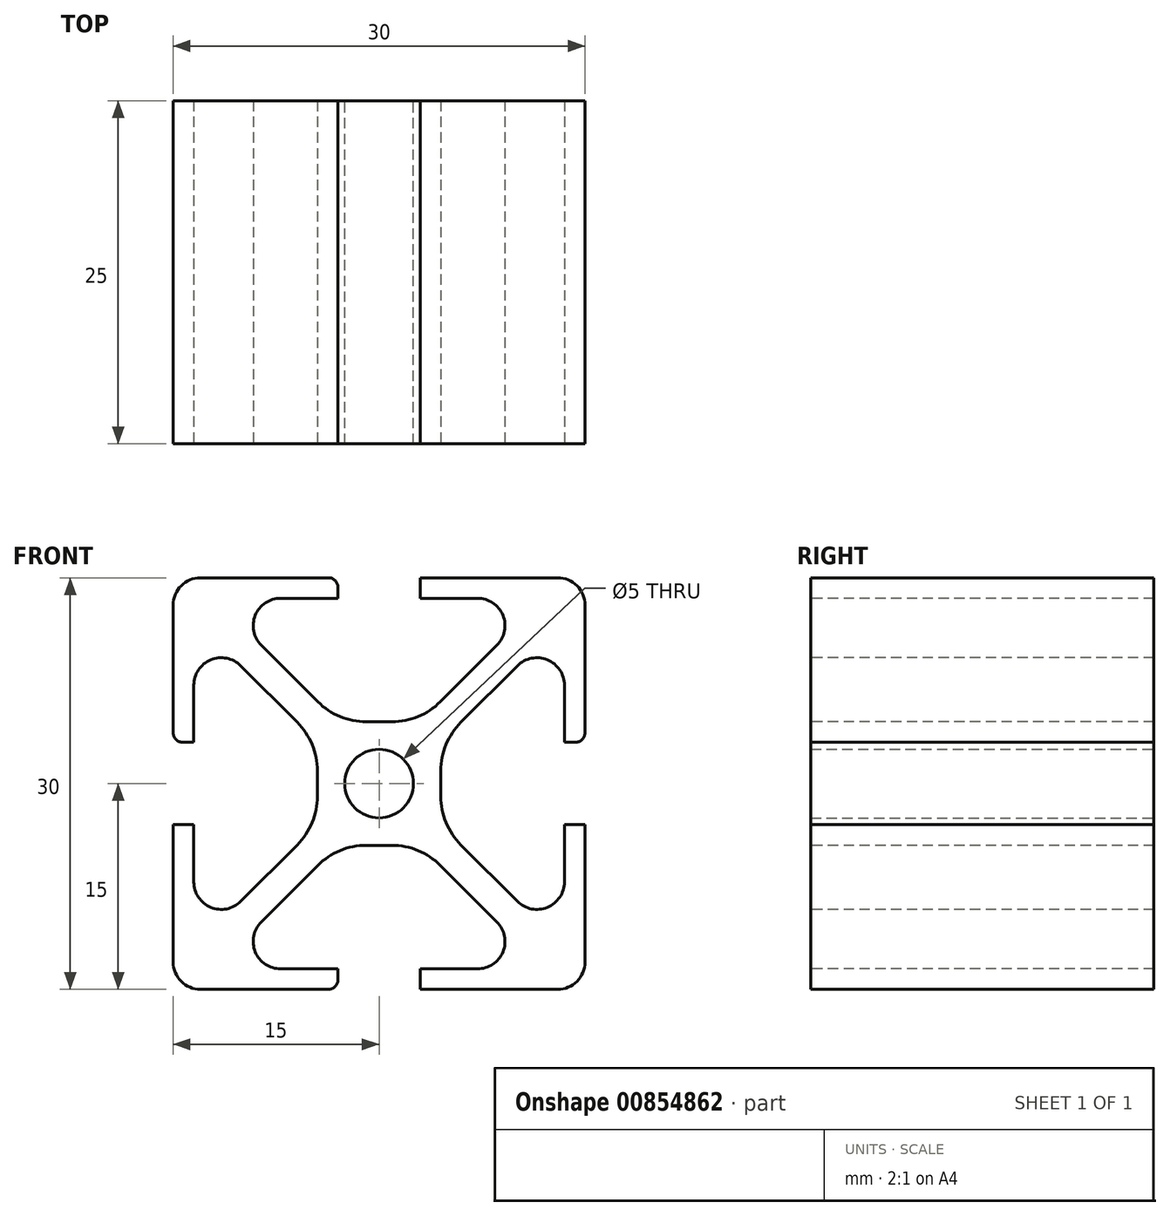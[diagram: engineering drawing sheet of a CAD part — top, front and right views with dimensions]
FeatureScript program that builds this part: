
annotation { "Feature Type Name" : "Feature", "Feature Type Description" : "" }
export const myFeature = defineFeature(function(context is Context, id is Id, definition is map)
    precondition{}
    {
        {
            var Q0;
            Q0=qCreatedBy(makeId("Front.planeOp"),FACE);
            var sketch = newSketch(context, id + "F0", { "sketchPlane" : qUnion([Q0])});
            skLineSegment(sketch, "E0.bottom", {"start": v(15, -15) * mm, "end": v(-15, -15) * mm});
            skLineSegment(sketch, "E0.top", {"start": v(15, 15) * mm, "end": v(-15, 15) * mm});
            skLineSegment(sketch, "E0.left", {"start": v(15, -15) * mm, "end": v(15, 15) * mm});
            skLineSegment(sketch, "E0.right", {"start": v(-15, -15) * mm, "end": v(-15, 15) * mm});
            skPoint(sketch, "E0.middle", {"position": v(0, 0) * mm});
            skCircle(sketch, "E1", {"center": v(0, 0) * mm, "radius": 2.5 * mm});
            skSolve(sketch);
        }
        {
            var Q0;
            Q0=qSketchRegion(id+"F0",true);
            extrude(context, id + "F1", {"entities" : qUnion([Q0]), "endBound" : BoundingType.SYMMETRIC, "depth" : 25 * mm, "offsetDistance" : 25 * mm});
        }
        {
            var Q0;
            Q0=makeQuery(id+"F1.opExtrude","SWEPT_EDGE",EDGE,{"disambiguationData":[OSD([sQuery(id+"F0.wireOp",EDGE,"E0.top"),sQuery(id+"F0.wireOp",EDGE,"E0.left")])]});
            var Q1;
            Q1=makeQuery(id+"F1.opExtrude","SWEPT_EDGE",EDGE,{"disambiguationData":[OSD([sQuery(id+"F0.wireOp",EDGE,"E0.top"),sQuery(id+"F0.wireOp",EDGE,"E0.right")])]});
            var Q2;
            Q2=makeQuery(id+"F1.opExtrude","SWEPT_EDGE",EDGE,{"disambiguationData":[OSD([sQuery(id+"F0.wireOp",EDGE,"E0.bottom"),sQuery(id+"F0.wireOp",EDGE,"E0.right")])]});
            var Q3;
            Q3=makeQuery(id+"F1.opExtrude","SWEPT_EDGE",EDGE,{"disambiguationData":[OSD([sQuery(id+"F0.wireOp",EDGE,"E0.bottom"),sQuery(id+"F0.wireOp",EDGE,"E0.left")])]});
            fillet(context, id + "F2", {"entities" : qUnion([Q0, Q1, Q2, Q3]), "radius" : 2 * mm, "tangentPropagation" : true, "allowEdgeOverflow" : false});
        }
        {
            var Q0;
            Q0=makeQuery(id+"F1.opExtrude","CAP_FACE",FACE,{"disambiguationData":[OSD([sQuery(id+"F0.wireOp",EDGE,"E0.bottom"),sQuery(id+"F0.wireOp",EDGE,"E0.top"),sQuery(id+"F0.wireOp",EDGE,"E0.left"),sQuery(id+"F0.wireOp",EDGE,"E0.right"),sQuery(id+"F0.wireOp",EDGE,"E1")])],"isStart":false});
            var sketch = newSketch(context, id + "F3", { "sketchPlane" : qUnion([Q0])});
            skPoint(sketch, "E2.middle", {"position": v(0, 0) * mm});
            skLineSegment(sketch, "E3.left", {"start": v(4.5, 3) * mm, "end": v(4.5, -3) * mm});
            skLineSegment(sketch, "E4.bottom", {"start": v(-3, 4.5) * mm, "end": v(3, 4.5) * mm});
            skLineSegment(sketch, "E4.top", {"start": v(-3, 15) * mm, "end": v(3, 15) * mm});
            skLineSegment(sketch, "E4.left", {"start": v(-3, 4.5) * mm, "end": v(-3, 15) * mm});
            skLineSegment(sketch, "E4.right", {"start": v(3, 4.5) * mm, "end": v(3, 15) * mm});
            skLineSegment(sketch, "E5.bottom", {"start": v(4.5, 3) * mm, "end": v(15, 3) * mm});
            skLineSegment(sketch, "E5.top", {"start": v(4.5, -3) * mm, "end": v(15, -3) * mm});
            skLineSegment(sketch, "E5.right", {"start": v(15, 3) * mm, "end": v(15, -3) * mm});
            skLineSegment(sketch, "E6.bottom", {"start": v(3, -4.5) * mm, "end": v(-3, -4.5) * mm});
            skLineSegment(sketch, "E6.top", {"start": v(3, -15) * mm, "end": v(-3, -15) * mm});
            skLineSegment(sketch, "E6.left", {"start": v(3, -4.5) * mm, "end": v(3, -15) * mm});
            skLineSegment(sketch, "E6.right", {"start": v(-3, -4.5) * mm, "end": v(-3, -15) * mm});
            skLineSegment(sketch, "E7.bottom", {"start": v(-4.5, -3) * mm, "end": v(-15, -3) * mm});
            skLineSegment(sketch, "E7.top", {"start": v(-4.5, 3) * mm, "end": v(-15, 3) * mm});
            skLineSegment(sketch, "E7.left", {"start": v(-4.5, -3) * mm, "end": v(-4.5, 3) * mm});
            skLineSegment(sketch, "E7.right", {"start": v(-15, -3) * mm, "end": v(-15, 3) * mm});
            skSolve(sketch);
        }
        {
            var Q0;
            Q0=qSketchRegion(id+"F3",true);
            extrude(context, id + "F4", {"entities" : qUnion([Q0]), "operationType" : NewBodyOperationType.REMOVE, "oppositeDirection" : true, "depth" : 25 * mm, "offsetDistance" : 25 * mm});
        }
        {
            var Q0;
            Q0=qSketchRegion(id+"F3",true);
            extrude(context, id + "F5", {"entities" : qUnion([Q0]), "operationType" : NewBodyOperationType.REMOVE, "oppositeDirection" : true, "depth" : 25 * mm, "offsetDistance" : 25 * mm});
        }
        {
            var Q0;
            Q0=makeQuery(id+"F1.opExtrude","CAP_FACE",FACE,{"disambiguationData":[OSD([sQuery(id+"F0.wireOp",EDGE,"E0.bottom"),sQuery(id+"F0.wireOp",EDGE,"E0.top"),sQuery(id+"F0.wireOp",EDGE,"E0.left"),sQuery(id+"F0.wireOp",EDGE,"E0.right"),sQuery(id+"F0.wireOp",EDGE,"E1")])],"isStart":false});
            var sketch = newSketch(context, id + "F6", { "sketchPlane" : qUnion([Q0])});
            skPoint(sketch, "E8.middle", {"position": v(0, 0) * mm});
            skPoint(sketch, "E9.middle", {"position": v(9, 9) * mm});
            skLineSegment(sketch, "E10", {"start": v(3, 4.5) * mm, "end": v(12, 13.5) * mm});
            skLineSegment(sketch, "E11", {"start": v(4.5, 3) * mm, "end": v(13.5, 12) * mm});
            skLineSegment(sketch, "E12", {"start": v(13.5, 3) * mm, "end": v(13.5, 12) * mm});
            skLineSegment(sketch, "E13", {"start": v(3, 13.5) * mm, "end": v(12, 13.5) * mm});
            skLineSegment(sketch, "E14.MirrorCS", {"start": v(3, -13.5) * mm, "end": v(12, -13.5) * mm});
            skLineSegment(sketch, "E15.MirrorCS", {"start": v(3, -4.5) * mm, "end": v(12, -13.5) * mm});
            skLineSegment(sketch, "E16.MirrorCS", {"start": v(4.5, -3) * mm, "end": v(13.5, -12) * mm});
            skLineSegment(sketch, "E17.MirrorCS", {"start": v(13.5, -3) * mm, "end": v(13.5, -12) * mm});
            skLineSegment(sketch, "E18.MirrorCS", {"start": v(-3, 13.5) * mm, "end": v(-12, 13.5) * mm});
            skLineSegment(sketch, "E19.MirrorCS", {"start": v(-3, 4.5) * mm, "end": v(-12, 13.5) * mm});
            skLineSegment(sketch, "E20.MirrorCS", {"start": v(-4.5, 3) * mm, "end": v(-13.5, 12) * mm});
            skLineSegment(sketch, "E21.MirrorCS", {"start": v(-13.5, 3) * mm, "end": v(-13.5, 12) * mm});
            skLineSegment(sketch, "E22.MirrorCS", {"start": v(-4.5, -3) * mm, "end": v(-13.5, -12) * mm});
            skLineSegment(sketch, "E23.MirrorCS", {"start": v(-3, -4.5) * mm, "end": v(-12, -13.5) * mm});
            skLineSegment(sketch, "E24.MirrorCS", {"start": v(-3, -13.5) * mm, "end": v(-12, -13.5) * mm});
            skLineSegment(sketch, "E25.MirrorCS", {"start": v(-13.5, -3) * mm, "end": v(-13.5, -12) * mm});
            skLineSegment(sketch, "E26", {"start": v(-13.5, 3) * mm, "end": v(-4.5, 3) * mm});
            skLineSegment(sketch, "E27", {"start": v(-3, 4.5) * mm, "end": v(-3, 13.5) * mm});
            skLineSegment(sketch, "E28", {"start": v(3, 13.5) * mm, "end": v(3, 4.5) * mm});
            skLineSegment(sketch, "E29", {"start": v(4.5, 3) * mm, "end": v(13.5, 3) * mm});
            skLineSegment(sketch, "E30", {"start": v(13.5, -3) * mm, "end": v(4.5, -3) * mm});
            skLineSegment(sketch, "E31", {"start": v(3, -4.5) * mm, "end": v(3, -13.5) * mm});
            skLineSegment(sketch, "E32", {"start": v(-3, -13.5) * mm, "end": v(-3, -4.5) * mm});
            skLineSegment(sketch, "E33", {"start": v(-4.5, -3) * mm, "end": v(-13.5, -3) * mm});
            skSolve(sketch);
        }
        {
            var Q0;
            Q0=qSketchRegion(id+"F6",true);
            extrude(context, id + "F7", {"entities" : qUnion([Q0]), "operationType" : NewBodyOperationType.REMOVE, "oppositeDirection" : true, "depth" : 25 * mm, "offsetDistance" : 25 * mm});
        }
        {
            var Q0;
            Q0=makeQuery(id+"F7.boolean.opBoolean","COPY",EDGE,{"derivedFrom":makeQuery(id+"F7.opExtrude","SWEPT_EDGE",EDGE,{"disambiguationData":[OSD([sQuery(id+"F6.wireOp",EDGE,"E23.MirrorCS"),sQuery(id+"F6.wireOp",EDGE,"E24.MirrorCS")])]})});
            var Q1;
            Q1=makeQuery(id+"F7.boolean.opBoolean","COPY",EDGE,{"derivedFrom":makeQuery(id+"F7.opExtrude","SWEPT_EDGE",EDGE,{"disambiguationData":[OSD([sQuery(id+"F6.wireOp",EDGE,"E14.MirrorCS"),sQuery(id+"F6.wireOp",EDGE,"E15.MirrorCS")])]})});
            var Q2;
            Q2=makeQuery(id+"F7.boolean.opBoolean","COPY",EDGE,{"derivedFrom":makeQuery(id+"F7.opExtrude","SWEPT_EDGE",EDGE,{"disambiguationData":[OSD([sQuery(id+"F6.wireOp",EDGE,"E16.MirrorCS"),sQuery(id+"F6.wireOp",EDGE,"E17.MirrorCS")])]})});
            var Q3;
            Q3=makeQuery(id+"F7.boolean.opBoolean","COPY",EDGE,{"derivedFrom":makeQuery(id+"F7.opExtrude","SWEPT_EDGE",EDGE,{"disambiguationData":[OSD([sQuery(id+"F6.wireOp",EDGE,"E22.MirrorCS"),sQuery(id+"F6.wireOp",EDGE,"E25.MirrorCS")])]})});
            var Q4;
            Q4=makeQuery(id+"F7.boolean.opBoolean","COPY",EDGE,{"derivedFrom":makeQuery(id+"F7.opExtrude","SWEPT_EDGE",EDGE,{"disambiguationData":[OSD([sQuery(id+"F6.wireOp",EDGE,"E11"),sQuery(id+"F6.wireOp",EDGE,"E12")])]})});
            var Q5;
            Q5=makeQuery(id+"F7.boolean.opBoolean","COPY",EDGE,{"derivedFrom":makeQuery(id+"F7.opExtrude","SWEPT_EDGE",EDGE,{"disambiguationData":[OSD([sQuery(id+"F6.wireOp",EDGE,"E10"),sQuery(id+"F6.wireOp",EDGE,"E13")])]})});
            var Q6;
            Q6=makeQuery(id+"F7.boolean.opBoolean","COPY",EDGE,{"derivedFrom":makeQuery(id+"F7.opExtrude","SWEPT_EDGE",EDGE,{"disambiguationData":[OSD([sQuery(id+"F6.wireOp",EDGE,"E20.MirrorCS"),sQuery(id+"F6.wireOp",EDGE,"E21.MirrorCS")])]})});
            var Q7;
            Q7=makeQuery(id+"F7.boolean.opBoolean","COPY",EDGE,{"derivedFrom":makeQuery(id+"F7.opExtrude","SWEPT_EDGE",EDGE,{"disambiguationData":[OSD([sQuery(id+"F6.wireOp",EDGE,"E18.MirrorCS"),sQuery(id+"F6.wireOp",EDGE,"E19.MirrorCS")])]})});
            fillet(context, id + "F8", {"entities" : qUnion([Q0, Q1, Q2, Q3, Q4, Q5, Q6, Q7]), "radius" : 2 * mm, "tangentPropagation" : true, "allowEdgeOverflow" : false});
        }
        {
            var Q0;
            Q0=makeQuery(id+"F7.boolean.opBoolean","COPY",EDGE,{"derivedFrom":makeQuery(id+"F7.opExtrude","SWEPT_EDGE",EDGE,{"disambiguationData":[OSD([sQuery(id+"F3.wireOp",EDGE,"E5.bottom"),sQuery(id+"F6.wireOp",EDGE,"E12"),sQuery(id+"F6.wireOp",EDGE,"E29")])]})});
            var Q1;
            Q1=makeQuery(id+"F4.boolean.opBoolean","COPY",EDGE,{"derivedFrom":makeQuery(id+"F4.opExtrude","SWEPT_EDGE",EDGE,{"disambiguationData":[OSD([sQuery(id+"F0.wireOp",EDGE,"E0.left"),sQuery(id+"F3.wireOp",EDGE,"E5.bottom"),sQuery(id+"F3.wireOp",EDGE,"E5.right")])]})});
            var Q2;
            Q2=makeQuery(id+"F4.boolean.opBoolean","COPY",EDGE,{"derivedFrom":makeQuery(id+"F4.opExtrude","SWEPT_EDGE",EDGE,{"disambiguationData":[OSD([sQuery(id+"F0.wireOp",EDGE,"E0.left"),sQuery(id+"F3.wireOp",EDGE,"E5.top"),sQuery(id+"F3.wireOp",EDGE,"E5.right")])]})});
            var Q3;
            Q3=makeQuery(id+"F7.boolean.opBoolean","COPY",EDGE,{"derivedFrom":makeQuery(id+"F7.opExtrude","SWEPT_EDGE",EDGE,{"disambiguationData":[OSD([sQuery(id+"F3.wireOp",EDGE,"E5.top"),sQuery(id+"F6.wireOp",EDGE,"E17.MirrorCS"),sQuery(id+"F6.wireOp",EDGE,"E30")])]})});
            var Q4;
            Q4=makeQuery(id+"F4.boolean.opBoolean","COPY",EDGE,{"derivedFrom":makeQuery(id+"F4.opExtrude","SWEPT_EDGE",EDGE,{"disambiguationData":[OSD([sQuery(id+"F0.wireOp",EDGE,"E0.bottom"),sQuery(id+"F3.wireOp",EDGE,"E6.top"),sQuery(id+"F3.wireOp",EDGE,"E6.left")])]})});
            var Q5;
            Q5=makeQuery(id+"F4.boolean.opBoolean","COPY",EDGE,{"derivedFrom":makeQuery(id+"F4.opExtrude","SWEPT_EDGE",EDGE,{"disambiguationData":[OSD([sQuery(id+"F0.wireOp",EDGE,"E0.bottom"),sQuery(id+"F3.wireOp",EDGE,"E6.top"),sQuery(id+"F3.wireOp",EDGE,"E6.right")])]})});
            var Q6;
            Q6=makeQuery(id+"F7.boolean.opBoolean","COPY",EDGE,{"derivedFrom":makeQuery(id+"F7.opExtrude","SWEPT_EDGE",EDGE,{"disambiguationData":[OSD([sQuery(id+"F3.wireOp",EDGE,"E6.left"),sQuery(id+"F6.wireOp",EDGE,"E14.MirrorCS"),sQuery(id+"F6.wireOp",EDGE,"E31")])]})});
            var Q7;
            Q7=makeQuery(id+"F7.boolean.opBoolean","COPY",EDGE,{"derivedFrom":makeQuery(id+"F7.opExtrude","SWEPT_EDGE",EDGE,{"disambiguationData":[OSD([sQuery(id+"F3.wireOp",EDGE,"E6.right"),sQuery(id+"F6.wireOp",EDGE,"E24.MirrorCS"),sQuery(id+"F6.wireOp",EDGE,"E32")])]})});
            var Q8;
            Q8=makeQuery(id+"F4.boolean.opBoolean","COPY",EDGE,{"derivedFrom":makeQuery(id+"F4.opExtrude","SWEPT_EDGE",EDGE,{"disambiguationData":[OSD([sQuery(id+"F0.wireOp",EDGE,"E0.right"),sQuery(id+"F3.wireOp",EDGE,"E7.bottom"),sQuery(id+"F3.wireOp",EDGE,"E7.right")])]})});
            var Q9;
            Q9=makeQuery(id+"F7.boolean.opBoolean","COPY",EDGE,{"derivedFrom":makeQuery(id+"F7.opExtrude","SWEPT_EDGE",EDGE,{"disambiguationData":[OSD([sQuery(id+"F3.wireOp",EDGE,"E7.bottom"),sQuery(id+"F6.wireOp",EDGE,"E25.MirrorCS"),sQuery(id+"F6.wireOp",EDGE,"E33")])]})});
            var Q10;
            Q10=makeQuery(id+"F4.boolean.opBoolean","COPY",EDGE,{"derivedFrom":makeQuery(id+"F4.opExtrude","SWEPT_EDGE",EDGE,{"disambiguationData":[OSD([sQuery(id+"F0.wireOp",EDGE,"E0.right"),sQuery(id+"F3.wireOp",EDGE,"E7.top"),sQuery(id+"F3.wireOp",EDGE,"E7.right")])]})});
            var Q11;
            Q11=makeQuery(id+"F7.boolean.opBoolean","COPY",EDGE,{"derivedFrom":makeQuery(id+"F7.opExtrude","SWEPT_EDGE",EDGE,{"disambiguationData":[OSD([sQuery(id+"F3.wireOp",EDGE,"E7.top"),sQuery(id+"F6.wireOp",EDGE,"E21.MirrorCS"),sQuery(id+"F6.wireOp",EDGE,"E26")])]})});
            var Q12;
            Q12=makeQuery(id+"F7.boolean.opBoolean","COPY",EDGE,{"derivedFrom":makeQuery(id+"F7.opExtrude","SWEPT_EDGE",EDGE,{"disambiguationData":[OSD([sQuery(id+"F3.wireOp",EDGE,"E4.right"),sQuery(id+"F6.wireOp",EDGE,"E13"),sQuery(id+"F6.wireOp",EDGE,"E28")])]})});
            var Q13;
            Q13=makeQuery(id+"F4.boolean.opBoolean","COPY",EDGE,{"derivedFrom":makeQuery(id+"F4.opExtrude","SWEPT_EDGE",EDGE,{"disambiguationData":[OSD([sQuery(id+"F0.wireOp",EDGE,"E0.top"),sQuery(id+"F3.wireOp",EDGE,"E4.top"),sQuery(id+"F3.wireOp",EDGE,"E4.right")])]})});
            var Q14;
            Q14=makeQuery(id+"F4.boolean.opBoolean","COPY",EDGE,{"derivedFrom":makeQuery(id+"F4.opExtrude","SWEPT_EDGE",EDGE,{"disambiguationData":[OSD([sQuery(id+"F0.wireOp",EDGE,"E0.top"),sQuery(id+"F3.wireOp",EDGE,"E4.top"),sQuery(id+"F3.wireOp",EDGE,"E4.left")])]})});
            var Q15;
            Q15=makeQuery(id+"F7.boolean.opBoolean","COPY",EDGE,{"derivedFrom":makeQuery(id+"F7.opExtrude","SWEPT_EDGE",EDGE,{"disambiguationData":[OSD([sQuery(id+"F3.wireOp",EDGE,"E4.left"),sQuery(id+"F6.wireOp",EDGE,"E18.MirrorCS"),sQuery(id+"F6.wireOp",EDGE,"E27")])]})});
            fillet(context, id + "F9", {"entities" : qUnion([Q0, Q1, Q2, Q3, Q4, Q5, Q6, Q7, Q8, Q9, Q10, Q11, Q12, Q13, Q14, Q15]), "radius" : 0.7 * mm, "tangentPropagation" : true, "allowEdgeOverflow" : false});
        }
        {
            var Q0;
            {var subQ0=sQuery(id+"F3.wireOp",EDGE,"E3.left");Q0=makeQuery(id+"F7.boolean.opBoolean","MERGE",EDGE,{"derivedFrom":[makeQuery(id+"F4.boolean.opBoolean","COPY",EDGE,{"derivedFrom":makeQuery(id+"F4.opExtrude","SWEPT_EDGE",EDGE,{"disambiguationData":[OSD([sQuery(id+"F3.wireOp",EDGE,"E5.top"),subQ0])]})}),makeQuery(id+"F7.opExtrude","SWEPT_EDGE",EDGE,{"disambiguationData":[OSD([subQ0,sQuery(id+"F6.wireOp",EDGE,"E16.MirrorCS"),sQuery(id+"F6.wireOp",EDGE,"E30")])]})]});}
            var Q1;
            {var subQ0=sQuery(id+"F3.wireOp",EDGE,"E3.left");Q1=makeQuery(id+"F7.boolean.opBoolean","MERGE",EDGE,{"derivedFrom":[makeQuery(id+"F4.boolean.opBoolean","COPY",EDGE,{"derivedFrom":makeQuery(id+"F4.opExtrude","SWEPT_EDGE",EDGE,{"disambiguationData":[OSD([sQuery(id+"F3.wireOp",EDGE,"E5.bottom"),subQ0])]})}),makeQuery(id+"F7.opExtrude","SWEPT_EDGE",EDGE,{"disambiguationData":[OSD([subQ0,sQuery(id+"F6.wireOp",EDGE,"E11"),sQuery(id+"F6.wireOp",EDGE,"E29")])]})]});}
            var Q2;
            {var subQ0=sQuery(id+"F3.wireOp",EDGE,"E6.bottom");Q2=makeQuery(id+"F7.boolean.opBoolean","MERGE",EDGE,{"derivedFrom":[makeQuery(id+"F4.boolean.opBoolean","COPY",EDGE,{"derivedFrom":makeQuery(id+"F4.opExtrude","SWEPT_EDGE",EDGE,{"disambiguationData":[OSD([subQ0,sQuery(id+"F3.wireOp",EDGE,"E6.right")])]})}),makeQuery(id+"F7.opExtrude","SWEPT_EDGE",EDGE,{"disambiguationData":[OSD([subQ0,sQuery(id+"F6.wireOp",EDGE,"E23.MirrorCS"),sQuery(id+"F6.wireOp",EDGE,"E32")])]})]});}
            var Q3;
            {var subQ0=sQuery(id+"F3.wireOp",EDGE,"E6.bottom");Q3=makeQuery(id+"F7.boolean.opBoolean","MERGE",EDGE,{"derivedFrom":[makeQuery(id+"F4.boolean.opBoolean","COPY",EDGE,{"derivedFrom":makeQuery(id+"F4.opExtrude","SWEPT_EDGE",EDGE,{"disambiguationData":[OSD([subQ0,sQuery(id+"F3.wireOp",EDGE,"E6.left")])]})}),makeQuery(id+"F7.opExtrude","SWEPT_EDGE",EDGE,{"disambiguationData":[OSD([subQ0,sQuery(id+"F6.wireOp",EDGE,"E15.MirrorCS"),sQuery(id+"F6.wireOp",EDGE,"E31")])]})]});}
            var Q4;
            {var subQ0=sQuery(id+"F3.wireOp",EDGE,"E7.left");Q4=makeQuery(id+"F7.boolean.opBoolean","MERGE",EDGE,{"derivedFrom":[makeQuery(id+"F4.boolean.opBoolean","COPY",EDGE,{"derivedFrom":makeQuery(id+"F4.opExtrude","SWEPT_EDGE",EDGE,{"disambiguationData":[OSD([sQuery(id+"F3.wireOp",EDGE,"E7.bottom"),subQ0])]})}),makeQuery(id+"F7.opExtrude","SWEPT_EDGE",EDGE,{"disambiguationData":[OSD([subQ0,sQuery(id+"F6.wireOp",EDGE,"E22.MirrorCS"),sQuery(id+"F6.wireOp",EDGE,"E33")])]})]});}
            var Q5;
            {var subQ0=sQuery(id+"F3.wireOp",EDGE,"E7.left");Q5=makeQuery(id+"F7.boolean.opBoolean","MERGE",EDGE,{"derivedFrom":[makeQuery(id+"F4.boolean.opBoolean","COPY",EDGE,{"derivedFrom":makeQuery(id+"F4.opExtrude","SWEPT_EDGE",EDGE,{"disambiguationData":[OSD([sQuery(id+"F3.wireOp",EDGE,"E7.top"),subQ0])]})}),makeQuery(id+"F7.opExtrude","SWEPT_EDGE",EDGE,{"disambiguationData":[OSD([subQ0,sQuery(id+"F6.wireOp",EDGE,"E20.MirrorCS"),sQuery(id+"F6.wireOp",EDGE,"E26")])]})]});}
            var Q6;
            {var subQ0=sQuery(id+"F3.wireOp",EDGE,"E4.bottom");Q6=makeQuery(id+"F7.boolean.opBoolean","MERGE",EDGE,{"derivedFrom":[makeQuery(id+"F4.boolean.opBoolean","COPY",EDGE,{"derivedFrom":makeQuery(id+"F4.opExtrude","SWEPT_EDGE",EDGE,{"disambiguationData":[OSD([subQ0,sQuery(id+"F3.wireOp",EDGE,"E4.right")])]})}),makeQuery(id+"F7.opExtrude","SWEPT_EDGE",EDGE,{"disambiguationData":[OSD([subQ0,sQuery(id+"F6.wireOp",EDGE,"E10"),sQuery(id+"F6.wireOp",EDGE,"E28")])]})]});}
            var Q7;
            {var subQ0=sQuery(id+"F3.wireOp",EDGE,"E4.bottom");Q7=makeQuery(id+"F7.boolean.opBoolean","MERGE",EDGE,{"derivedFrom":[makeQuery(id+"F4.boolean.opBoolean","COPY",EDGE,{"derivedFrom":makeQuery(id+"F4.opExtrude","SWEPT_EDGE",EDGE,{"disambiguationData":[OSD([subQ0,sQuery(id+"F3.wireOp",EDGE,"E4.left")])]})}),makeQuery(id+"F7.opExtrude","SWEPT_EDGE",EDGE,{"disambiguationData":[OSD([subQ0,sQuery(id+"F6.wireOp",EDGE,"E19.MirrorCS"),sQuery(id+"F6.wireOp",EDGE,"E27")])]})]});}
            fillet(context, id + "F10", {"entities" : qUnion([Q0, Q1, Q2, Q3, Q4, Q5, Q6, Q7]), "radius" : 5 * mm, "tangentPropagation" : true, "allowEdgeOverflow" : false});
        }
    });
